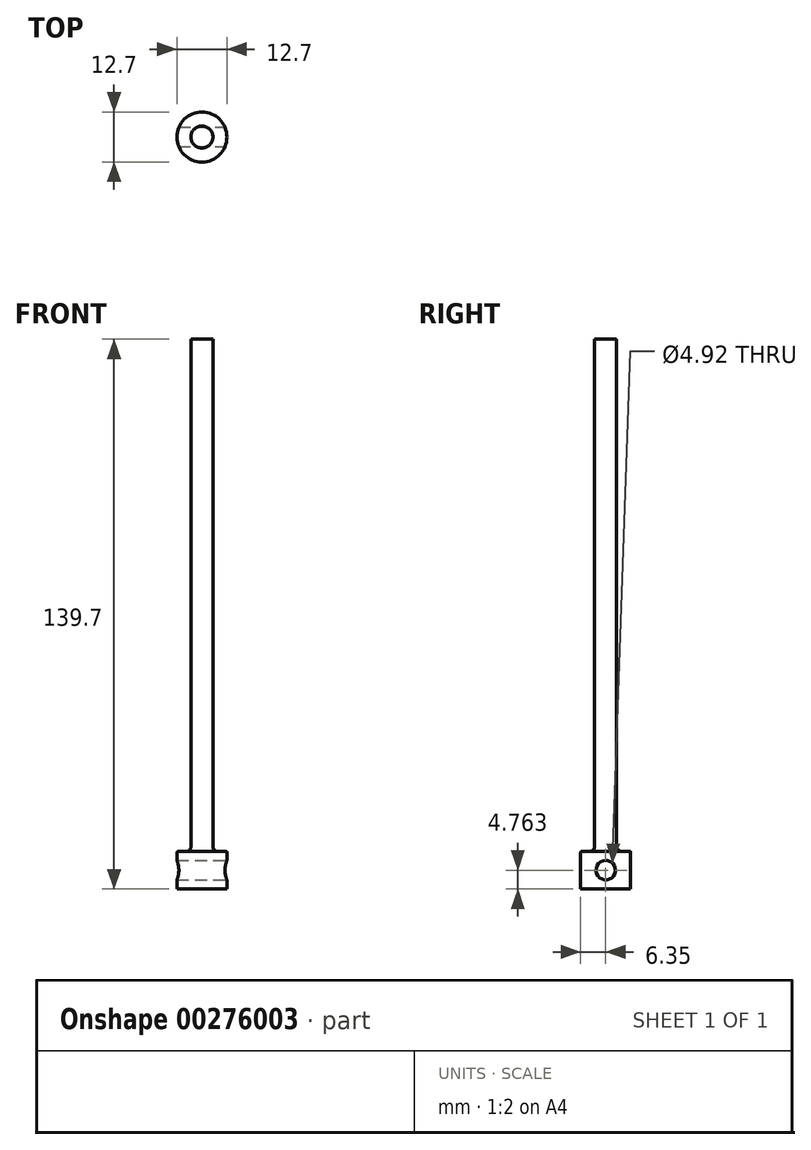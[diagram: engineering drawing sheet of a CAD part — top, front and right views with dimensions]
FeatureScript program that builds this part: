
annotation { "Feature Type Name" : "Feature", "Feature Type Description" : "" }
export const myFeature = defineFeature(function(context is Context, id is Id, definition is map)
    precondition{}
    {
        {
            var Q0;
            Q0=qCreatedBy(makeId("Top.planeOp"),FACE);
            var sketch = newSketch(context, id + "F0", { "sketchPlane" : qUnion([Q0])});
            skCircle(sketch, "E0", {"center": v(0, 0) * mm, "radius": 2.8 * mm});
            skSolve(sketch);
        }
        {
            var Q0;
            Q0 = qSketchRegion(id + "F0", true);
            extrude(context, id + "F1", {"entities" : qUnion([Q0]), "depth" : 139.7 * mm});
        }
        {
            var Q0;
            Q0=makeQuery(id+"F1.opExtrude","CAP_FACE",FACE,{"disambiguationData":[OSD([sQuery(id+"F0.wireOp",EDGE,"E0")])],"isStart":true});
            var sketch = newSketch(context, id + "F2", { "sketchPlane" : qUnion([Q0])});
            skCircle(sketch, "E1", {"center": v(0, 0) * mm, "radius": 6.35 * mm});
            skSolve(sketch);
        }
        {
            var Q0;
            Q0 = qSketchRegion(id + "F2", true);
            extrude(context, id + "F3", {"entities" : qUnion([Q0]), "operationType" : NewBodyOperationType.ADD, "oppositeDirection" : true, "depth" : 9.52 * mm});
        }
        {
            var Q0;
            Q0=makeQuery(id+"F3.boolean.opBoolean","INTERSECT",EDGE,{"derivedFrom":[makeQuery(id+"F1.opExtrude","SWEPT_FACE",FACE,{"disambiguationData":[OSD([sQuery(id+"F0.wireOp",EDGE,"E0")])]}),makeQuery(id+"F3.opExtrude","CAP_FACE",FACE,{"disambiguationData":[OSD([sQuery(id+"F2.wireOp",EDGE,"E1")])],"isStart":false})]});
            fillet(context, id + "F4", {"entities" : qUnion([Q0]), "radius" : 1.27 * mm, "tangentPropagation" : true, "allowEdgeOverflow" : false});
        }
        {
            var Q0;
            Q0=makeQuery(id+"F3.opExtrude","CAP_EDGE",EDGE,{"disambiguationData":[OSD([sQuery(id+"F2.wireOp",EDGE,"E1")])],"isStart":false});
            fillet(context, id + "F5", {"entities" : qUnion([Q0]), "radius" : 0.25 * mm, "tangentPropagation" : true, "allowEdgeOverflow" : false});
        }
        {
            var Q0;
            Q0=qCreatedBy(makeId("Right.planeOp"),FACE);
            var sketch = newSketch(context, id + "F6", { "sketchPlane" : qUnion([Q0])});
            skCircle(sketch, "E2", {"center": v(0, 4.76) * mm, "radius": 2.46 * mm});
            skSolve(sketch);
        }
        {
            var Q0;
            Q0 = qSketchRegion(id + "F6", true);
            extrude(context, id + "F7", {"entities" : qUnion([Q0]), "operationType" : NewBodyOperationType.REMOVE, "oppositeDirection" : true, "depth" : 25.4 * mm});
        }
        {
            var Q0;
            Q0 = qSketchRegion(id + "F6", true);
            extrude(context, id + "F8", {"entities" : qUnion([Q0]), "operationType" : NewBodyOperationType.REMOVE, "depth" : 25.4 * mm});
        }
    });
